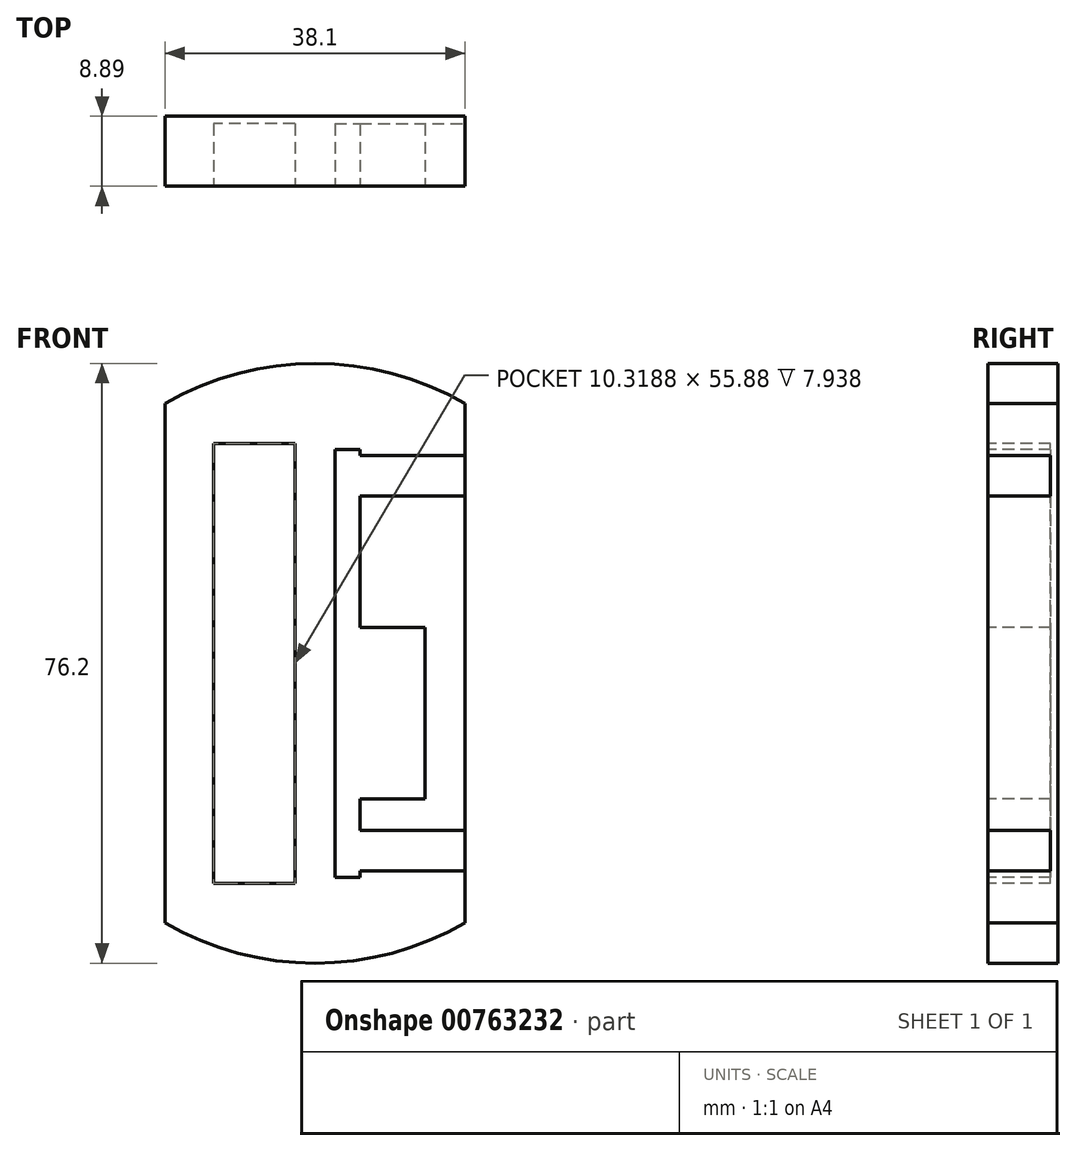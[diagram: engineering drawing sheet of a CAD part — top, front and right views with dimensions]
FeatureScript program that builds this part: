
annotation { "Feature Type Name" : "Feature", "Feature Type Description" : "" }
export const myFeature = defineFeature(function(context is Context, id is Id, definition is map)
    precondition{}
    {
        {
            var Q0;
            Q0=qCreatedBy(makeId("Front.planeOp"),FACE);
            var sketch = newSketch(context, id + "F0", { "sketchPlane" : qUnion([Q0])});
            skCircle(sketch, "E0", {"center": v(0, 0) * mm, "radius": 38.1 * mm});
            skSolve(sketch);
        }
        {
            var Q0;
            Q0=makeQuery(id+"F0.imprint","IMPRINT",FACE,{"disambiguationData":[TD([[makeQuery(id+"F0.imprint","IMPRINT",EDGE,{"derivedFrom":sQuery(id+"F0.wireOp",EDGE,"E0")}),1.0]])]});
            extrude(context, id + "F1", {"entities" : qUnion([Q0]), "depth" : 8.9 * mm, "offsetDistance" : 25.4 * mm});
        }
        {
            var Q0;
            Q0=makeQuery(id+"F1.opExtrude","CAP_FACE",FACE,{"disambiguationData":[OSD([sQuery(id+"F0.wireOp",EDGE,"E0")])],"isStart":false});
            var sketch = newSketch(context, id + "F2", { "sketchPlane" : qUnion([Q0])});
            skLineSegment(sketch, "E1.bottom", {"start": v(-2.54, -27.94) * mm, "end": v(-12.86, -27.94) * mm});
            skLineSegment(sketch, "E1.top", {"start": v(-2.54, 27.94) * mm, "end": v(-12.86, 27.94) * mm});
            skLineSegment(sketch, "E1.left", {"start": v(-2.54, -27.94) * mm, "end": v(-2.54, 27.94) * mm});
            skLineSegment(sketch, "E1.right", {"start": v(-12.86, -27.94) * mm, "end": v(-12.86, 27.94) * mm});
            skSolve(sketch);
        }
        {
            var Q0;
            Q0 = qSketchRegion(id + "F2", true);
            extrude(context, id + "F3", {"entities" : qUnion([Q0]), "operationType" : NewBodyOperationType.REMOVE, "oppositeDirection" : true, "depth" : 7.94 * mm, "offsetDistance" : 25.4 * mm});
        }
        {
            var Q0;
            Q0=makeQuery(id+"F1.opExtrude","CAP_FACE",FACE,{"disambiguationData":[OSD([sQuery(id+"F0.wireOp",EDGE,"E0")])],"isStart":false});
            var sketch = newSketch(context, id + "F4", { "sketchPlane" : qUnion([Q0])});
            skLineSegment(sketch, "E2.bottom", {"start": v(2.54, 27.18) * mm, "end": v(5.72, 27.18) * mm});
            skLineSegment(sketch, "E2.top", {"start": v(2.54, -27.18) * mm, "end": v(5.72, -27.18) * mm});
            skLineSegment(sketch, "E2.left", {"start": v(2.54, 27.18) * mm, "end": v(2.54, -27.18) * mm});
            skLineSegment(sketch, "E2.right", {"start": v(5.72, 27.18) * mm, "end": v(5.72, 26.38) * mm});
            skLineSegment(sketch, "E3.bottom", {"start": v(5.71, 26.38) * mm, "end": v(12.12, 26.38) * mm});
            skLineSegment(sketch, "E3.top", {"start": v(5.71, 21.22) * mm, "end": v(13.97, 21.22) * mm});
            skLineSegment(sketch, "E4.MirrorCS", {"start": v(5.71, -26.38) * mm, "end": v(12.12, -26.38) * mm});
            skLineSegment(sketch, "E5.MirrorCS", {"start": v(5.71, -21.22) * mm, "end": v(13.97, -21.22) * mm});
            skLineSegment(sketch, "E6.bottom", {"start": v(5.72, 4.57) * mm, "end": v(13.97, 4.57) * mm});
            skLineSegment(sketch, "E6.top", {"start": v(5.72, -17.26) * mm, "end": v(13.97, -17.26) * mm});
            skLineSegment(sketch, "E6.right", {"start": v(13.97, 4.57) * mm, "end": v(13.97, -17.26) * mm});
            skLineSegment(sketch, "E7.trimOffspring", {"start": v(5.72, 21.22) * mm, "end": v(5.72, 4.57) * mm});
            skLineSegment(sketch, "E8.trimOffspring", {"start": v(5.72, -17.26) * mm, "end": v(5.72, -21.22) * mm});
            skPoint(sketch, "E9.MirrorCS.end.orphan", {"position": v(5.71, -21.22) * mm});
            skPoint(sketch, "E9.MirrorCS.start.orphan", {"position": v(5.72, -26.38) * mm});
            skLineSegment(sketch, "E10.trimOffspring", {"start": v(5.72, -26.38) * mm, "end": v(5.72, -27.18) * mm});
            skLineSegment(sketch, "E11.bottom", {"start": v(12.12, 26.38) * mm, "end": v(32.34, 26.38) * mm});
            skLineSegment(sketch, "E11.top", {"start": v(12.12, 21.22) * mm, "end": v(32.34, 21.22) * mm});
            skLineSegment(sketch, "E11.right", {"start": v(32.34, 26.38) * mm, "end": v(32.34, 21.22) * mm});
            skLineSegment(sketch, "E12.MirrorCS", {"start": v(12.12, -21.22) * mm, "end": v(32.34, -21.22) * mm});
            skLineSegment(sketch, "E13.MirrorCS", {"start": v(12.12, -26.38) * mm, "end": v(32.34, -26.38) * mm});
            skLineSegment(sketch, "E14.MirrorCS", {"start": v(32.34, -26.38) * mm, "end": v(32.34, -21.22) * mm});
            skPoint(sketch, "E15.MirrorCS.end.orphan", {"position": v(13.97, -21.22) * mm});
            skPoint(sketch, "E15.MirrorCS.start.orphan", {"position": v(12.12, -26.38) * mm});
            skSolve(sketch);
        }
        {
            var Q0;
            Q0=makeQuery(id+"F4.imprint","IMPRINT",FACE,{"disambiguationData":[TD([[makeQuery(id+"F4.imprint","IMPRINT",EDGE,{"derivedFrom":sQuery(id+"F4.wireOp",EDGE,"E2.bottom")}),-1.0]])]});
            extrude(context, id + "F5", {"entities" : qUnion([Q0]), "operationType" : NewBodyOperationType.REMOVE, "oppositeDirection" : true, "depth" : 7.94 * mm, "offsetDistance" : 25.4 * mm});
        }
        {
            var Q0;
            Q0=makeQuery(id+"F1.opExtrude","CAP_FACE",FACE,{"disambiguationData":[OSD([sQuery(id+"F0.wireOp",EDGE,"E0")])],"isStart":false});
            var sketch = newSketch(context, id + "F6", { "sketchPlane" : qUnion([Q0])});
            skLineSegment(sketch, "E16.bottom", {"start": v(19.05, 53.44) * mm, "end": v(58.82, 53.44) * mm});
            skLineSegment(sketch, "E16.top", {"start": v(19.05, -55.42) * mm, "end": v(58.82, -55.42) * mm});
            skLineSegment(sketch, "E16.left", {"start": v(19.05, 53.44) * mm, "end": v(19.05, -55.42) * mm});
            skLineSegment(sketch, "E16.right", {"start": v(58.82, 53.44) * mm, "end": v(58.82, -55.42) * mm});
            skLineSegment(sketch, "E17.MirrorCS", {"start": v(-19.05, 53.44) * mm, "end": v(-19.05, -55.42) * mm});
            skLineSegment(sketch, "E18.MirrorCS", {"start": v(-19.05, 53.44) * mm, "end": v(-58.82, 53.44) * mm});
            skLineSegment(sketch, "E19.MirrorCS", {"start": v(-58.82, 53.44) * mm, "end": v(-58.82, -55.42) * mm});
            skLineSegment(sketch, "E20.MirrorCS", {"start": v(-19.05, -55.42) * mm, "end": v(-58.82, -55.42) * mm});
            skSolve(sketch);
        }
        {
            var Q0;
            Q0 = qSketchRegion(id + "F6", true);
            extrude(context, id + "F7", {"entities" : qUnion([Q0]), "operationType" : NewBodyOperationType.REMOVE, "oppositeDirection" : true, "depth" : 25.4 * mm, "offsetDistance" : 25.4 * mm});
        }
    });
